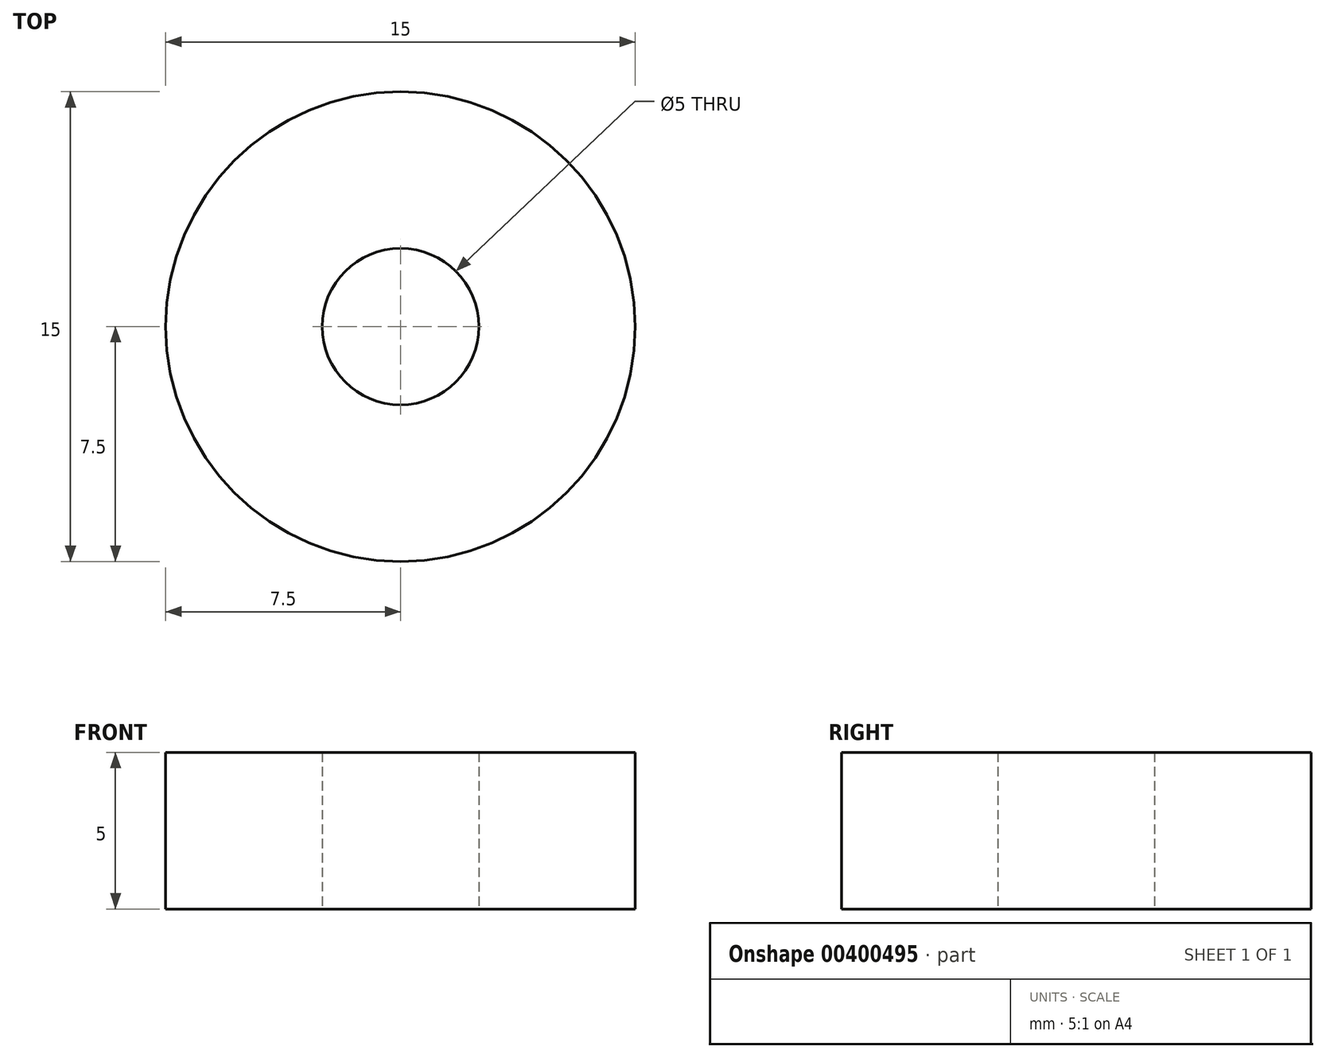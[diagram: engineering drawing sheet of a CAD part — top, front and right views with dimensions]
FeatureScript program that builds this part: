
annotation { "Feature Type Name" : "Feature", "Feature Type Description" : "" }
export const myFeature = defineFeature(function(context is Context, id is Id, definition is map)
    precondition{}
    {
        {
            var Q0;
            Q0=qCreatedBy(makeId("Top.planeOp"),FACE);
            var sketch = newSketch(context, id + "F0", { "sketchPlane" : qUnion([Q0])});
            skCircle(sketch, "E0", {"center": v(0, 0) * mm, "radius": 7.5 * mm});
            skSolve(sketch);
        }
        {
            var Q0;
            Q0=makeQuery(id+"F0.imprint","IMPRINT",FACE,{"disambiguationData":[TD([[makeQuery(id+"F0.imprint","IMPRINT",EDGE,{"derivedFrom":sQuery(id+"F0.wireOp",EDGE,"E0")}),1.0]])]});
            var sketch = newSketch(context, id + "F1", { "sketchPlane" : qUnion([Q0])});
            skCircle(sketch, "E1", {"center": v(0, 0) * mm, "radius": 2.5 * mm});
            skSolve(sketch);
        }
        {
            var Q0;
            Q0=makeQuery(id+"F1.imprint","IMPRINT",FACE,{"disambiguationData":[TD([[makeQuery(id+"F1.imprint","IMPRINT",EDGE,{"derivedFrom":sQuery(id+"F1.wireOp",EDGE,"E1")}),-1.0]])]});
            extrude(context, id + "F2", {"entities" : qUnion([Q0]), "depth" : 5 * mm});
        }
    });
